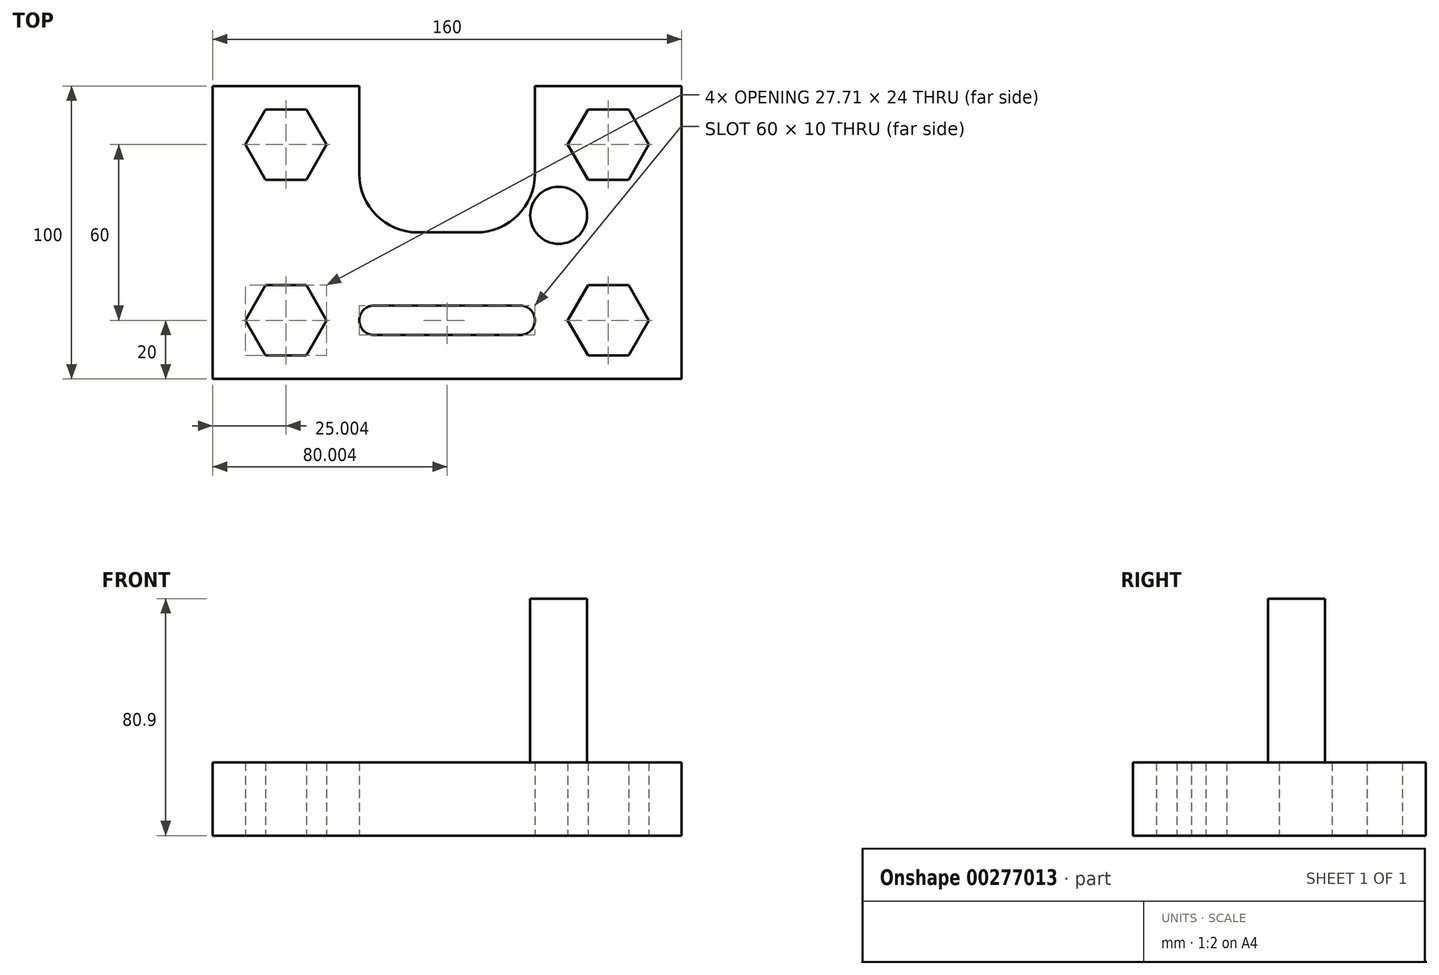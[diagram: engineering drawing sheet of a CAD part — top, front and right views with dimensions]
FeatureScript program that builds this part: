
annotation { "Feature Type Name" : "Feature", "Feature Type Description" : "" }
export const myFeature = defineFeature(function(context is Context, id is Id, definition is map)
    precondition{}
    {
        {
            var Q0;
            Q0=qCreatedBy(makeId("Top.planeOp"),FACE);
            var sketch = newSketch(context, id + "F0", { "sketchPlane" : qUnion([Q0])});
            skLineSegment(sketch, "E0", {"start": v(-72.62, -32.1) * mm, "end": v(-22.62, -32.1) * mm});
            skLineSegment(sketch, "E1", {"start": v(37.38, -32.1) * mm, "end": v(87.38, -32.1) * mm});
            skLineSegment(sketch, "E2", {"start": v(87.38, -32.1) * mm, "end": v(87.38, -132.1) * mm});
            skLineSegment(sketch, "E3", {"start": v(-72.62, -112.1) * mm, "end": v(-72.62, -32.1) * mm});
            skLineSegment(sketch, "E4", {"start": v(-22.62, -32.1) * mm, "end": v(-22.62, -62.1) * mm});
            skLineSegment(sketch, "E5", {"start": v(-2.62, -82.1) * mm, "end": v(17.38, -82.1) * mm});
            skLineSegment(sketch, "E6", {"start": v(37.38, -62.1) * mm, "end": v(37.38, -32.1) * mm});
            skPoint(sketch, "E7.visualSharp", {"position": v(37.38, -82.1) * mm});
            skArc(sketch, "E7.filletArc", {"start": v(17.38, -82.1) * mm, "mid": v(31.53, -76.23) * mm, "end": v(37.38, -62.1) * mm});
            skPoint(sketch, "E8.visualSharp", {"position": v(-22.62, -82.1) * mm});
            skArc(sketch, "E8.filletArc", {"start": v(-22.62, -62.1) * mm, "mid": v(-16.76, -76.23) * mm, "end": v(-2.62, -82.1) * mm});
            skLineSegment(sketch, "E9", {"start": v(87.38, -132.1) * mm, "end": v(87.38, -112.1) * mm});
            skCircle(sketch, "E10", {"center": v(62.38, -112.1) * mm, "radius": 12 * mm});
            skLineSegment(sketch, "E11", {"start": v(-72.62, -132.1) * mm, "end": v(-72.62, -112.1) * mm});
            skCircle(sketch, "E12", {"center": v(-47.62, -112.1) * mm, "radius": 12 * mm});
            skLineSegment(sketch, "E13", {"start": v(87.38, -32.1) * mm, "end": v(62.38, -32.1) * mm});
            skLineSegment(sketch, "E14", {"start": v(87.38, -32.1) * mm, "end": v(87.38, -52.1) * mm});
            skCircle(sketch, "E15", {"center": v(-47.62, -52.1) * mm, "radius": 12 * mm});
            skCircle(sketch, "E16", {"center": v(62.38, -52.1) * mm, "radius": 12 * mm});
            skCircle(sketch, "E17.cCircle", {"center": v(-47.62, -52.1) * mm, "radius": 12 * mm, "construction": true});
            skLineSegment(sketch, "E17.0", {"start": v(-40.69, -64.1) * mm, "end": v(-54.54, -64.1) * mm});
            skLineSegment(sketch, "E17.1", {"start": v(-54.54, -64.1) * mm, "end": v(-61.47, -52.1) * mm});
            skLineSegment(sketch, "E17.2", {"start": v(-61.47, -52.1) * mm, "end": v(-54.54, -40.1) * mm});
            skLineSegment(sketch, "E17.3", {"start": v(-54.54, -40.1) * mm, "end": v(-40.69, -40.1) * mm});
            skLineSegment(sketch, "E17.4", {"start": v(-40.69, -40.1) * mm, "end": v(-33.76, -52.1) * mm});
            skLineSegment(sketch, "E17.5", {"start": v(-33.76, -52.1) * mm, "end": v(-40.69, -64.1) * mm});
            skPoint(sketch, "E17.0.midPoint", {"position": v(-47.62, -64.1) * mm});
            skCircle(sketch, "E18.cCircle", {"center": v(-47.62, -112.1) * mm, "radius": 12 * mm, "construction": true});
            skLineSegment(sketch, "E18.0", {"start": v(-40.69, -124.1) * mm, "end": v(-54.54, -124.1) * mm});
            skLineSegment(sketch, "E18.1", {"start": v(-54.54, -124.1) * mm, "end": v(-61.47, -112.1) * mm});
            skLineSegment(sketch, "E18.2", {"start": v(-61.47, -112.1) * mm, "end": v(-54.54, -100.1) * mm});
            skLineSegment(sketch, "E18.3", {"start": v(-54.54, -100.1) * mm, "end": v(-40.69, -100.1) * mm});
            skLineSegment(sketch, "E18.4", {"start": v(-40.69, -100.1) * mm, "end": v(-33.76, -112.1) * mm});
            skLineSegment(sketch, "E18.5", {"start": v(-33.76, -112.1) * mm, "end": v(-40.69, -124.1) * mm});
            skPoint(sketch, "E18.0.midPoint", {"position": v(-47.62, -124.1) * mm});
            skCircle(sketch, "E19.cCircle", {"center": v(62.38, -112.1) * mm, "radius": 12 * mm, "construction": true});
            skLineSegment(sketch, "E19.0", {"start": v(55.46, -100.1) * mm, "end": v(69.31, -100.1) * mm});
            skLineSegment(sketch, "E19.1", {"start": v(69.31, -100.1) * mm, "end": v(76.24, -112.1) * mm});
            skLineSegment(sketch, "E19.2", {"start": v(76.24, -112.1) * mm, "end": v(69.31, -124.1) * mm});
            skLineSegment(sketch, "E19.3", {"start": v(69.31, -124.1) * mm, "end": v(55.46, -124.1) * mm});
            skLineSegment(sketch, "E19.4", {"start": v(55.46, -124.1) * mm, "end": v(48.53, -112.1) * mm});
            skLineSegment(sketch, "E19.5", {"start": v(48.53, -112.1) * mm, "end": v(55.46, -100.1) * mm});
            skPoint(sketch, "E19.0.midPoint", {"position": v(62.38, -100.1) * mm});
            skCircle(sketch, "E20.cCircle", {"center": v(62.38, -52.1) * mm, "radius": 12 * mm, "construction": true});
            skLineSegment(sketch, "E20.0", {"start": v(55.46, -40.1) * mm, "end": v(69.31, -40.1) * mm});
            skLineSegment(sketch, "E20.1", {"start": v(69.31, -40.1) * mm, "end": v(76.24, -52.1) * mm});
            skLineSegment(sketch, "E20.2", {"start": v(76.24, -52.1) * mm, "end": v(69.31, -64.1) * mm});
            skLineSegment(sketch, "E20.3", {"start": v(69.31, -64.1) * mm, "end": v(55.46, -64.1) * mm});
            skLineSegment(sketch, "E20.4", {"start": v(55.46, -64.1) * mm, "end": v(48.53, -52.1) * mm});
            skLineSegment(sketch, "E20.5", {"start": v(48.53, -52.1) * mm, "end": v(55.46, -40.1) * mm});
            skPoint(sketch, "E20.0.midPoint", {"position": v(62.38, -40.1) * mm});
            skPoint(sketch, "E21.end.orphan", {"position": v(-47.62, -32.1) * mm});
            skPoint(sketch, "E22.end.orphan", {"position": v(-47.62, -132.1) * mm});
            skLineSegment(sketch, "E23", {"start": v(-72.62, -132.1) * mm, "end": v(87.38, -132.1) * mm});
            skLineSegment(sketch, "E24", {"start": v(-72.62, -132.1) * mm, "end": v(-17.62, -132.1) * mm});
            skArc(sketch, "E25", {"start": v(-17.62, -107.1) * mm, "mid": v(-22.62, -112.1) * mm, "end": v(-17.62, -117.1) * mm});
            skArc(sketch, "E26", {"start": v(32.38, -117.1) * mm, "mid": v(37.38, -112.1) * mm, "end": v(32.38, -107.1) * mm});
            skLineSegment(sketch, "E27", {"start": v(-17.62, -107.1) * mm, "end": v(32.38, -107.1) * mm});
            skLineSegment(sketch, "E28", {"start": v(32.38, -117.1) * mm, "end": v(-17.62, -117.1) * mm});
            skSolve(sketch);
        }
        {
            var Q0;
            Q0=makeQuery(id+"F0.imprint","IMPRINT",FACE,{"disambiguationData":[TD([[makeQuery(id+"F0.imprint","IMPRINT",EDGE,{"derivedFrom":sQuery(id+"F0.wireOp",EDGE,"E0")}),-1.0]])]});
            extrude(context, id + "F1", {"entities" : qUnion([Q0]), "depth" : 25 * mm});
        }
        {
            var Q0;
            Q0=makeQuery(id+"F1.opExtrude","CAP_FACE",FACE,{"disambiguationData":[OSD([sQuery(id+"F0.wireOp",EDGE,"E0"),sQuery(id+"F0.wireOp",EDGE,"E1"),sQuery(id+"F0.wireOp",EDGE,"E2"),sQuery(id+"F0.wireOp",EDGE,"E3"),sQuery(id+"F0.wireOp",EDGE,"E4"),sQuery(id+"F0.wireOp",EDGE,"E5"),sQuery(id+"F0.wireOp",EDGE,"E6"),sQuery(id+"F0.wireOp",EDGE,"E7.filletArc"),sQuery(id+"F0.wireOp",EDGE,"E8.filletArc"),sQuery(id+"F0.wireOp",EDGE,"E9"),sQuery(id+"F0.wireOp",EDGE,"E11"),sQuery(id+"F0.wireOp",EDGE,"E13"),sQuery(id+"F0.wireOp",EDGE,"E14"),sQuery(id+"F0.wireOp",EDGE,"E17.0"),sQuery(id+"F0.wireOp",EDGE,"E17.1"),sQuery(id+"F0.wireOp",EDGE,"E17.2"),sQuery(id+"F0.wireOp",EDGE,"E17.3"),sQuery(id+"F0.wireOp",EDGE,"E17.4"),sQuery(id+"F0.wireOp",EDGE,"E17.5"),sQuery(id+"F0.wireOp",EDGE,"E18.0"),sQuery(id+"F0.wireOp",EDGE,"E18.1"),sQuery(id+"F0.wireOp",EDGE,"E18.2"),sQuery(id+"F0.wireOp",EDGE,"E18.3"),sQuery(id+"F0.wireOp",EDGE,"E18.4"),sQuery(id+"F0.wireOp",EDGE,"E18.5"),sQuery(id+"F0.wireOp",EDGE,"E19.0"),sQuery(id+"F0.wireOp",EDGE,"E19.1"),sQuery(id+"F0.wireOp",EDGE,"E19.2"),sQuery(id+"F0.wireOp",EDGE,"E19.3"),sQuery(id+"F0.wireOp",EDGE,"E19.4"),sQuery(id+"F0.wireOp",EDGE,"E19.5"),sQuery(id+"F0.wireOp",EDGE,"E20.0"),sQuery(id+"F0.wireOp",EDGE,"E20.1"),sQuery(id+"F0.wireOp",EDGE,"E20.2"),sQuery(id+"F0.wireOp",EDGE,"E20.3"),sQuery(id+"F0.wireOp",EDGE,"E20.4"),sQuery(id+"F0.wireOp",EDGE,"E20.5"),sQuery(id+"F0.wireOp",EDGE,"E23"),sQuery(id+"F0.wireOp",EDGE,"E24"),sQuery(id+"F0.wireOp",EDGE,"E25"),sQuery(id+"F0.wireOp",EDGE,"E26"),sQuery(id+"F0.wireOp",EDGE,"E27"),sQuery(id+"F0.wireOp",EDGE,"E28")])],"isStart":false});
            var sketch = newSketch(context, id + "F2", { "sketchPlane" : qUnion([Q0])});
            skCircle(sketch, "E29", {"center": v(-45.33, -76.8) * mm, "radius": 9.97 * mm});
            skSolve(sketch);
        }
        {
            var Q0;
            Q0=makeQuery(id+"F2.imprint","IMPRINT",FACE,{"disambiguationData":[TD([[makeQuery(id+"F2.imprint","IMPRINT",EDGE,{"derivedFrom":sQuery(id+"F2.wireOp",EDGE,"E29")}),-1.0]])]});
            var sketch = newSketch(context, id + "F3", { "sketchPlane" : qUnion([Q0])});
            skCircle(sketch, "E30", {"center": v(45.45, -76.26) * mm, "radius": 9.72 * mm});
            skSolve(sketch);
        }
        {
            var Q0;
            Q0 = qSketchRegion(id + "F3", true);
            extrude(context, id + "F4", {"entities" : qUnion([Q0]), "operationType" : NewBodyOperationType.ADD, "depth" : 55.9 * mm, "offsetDistance" : 25 * mm});
        }
    });
